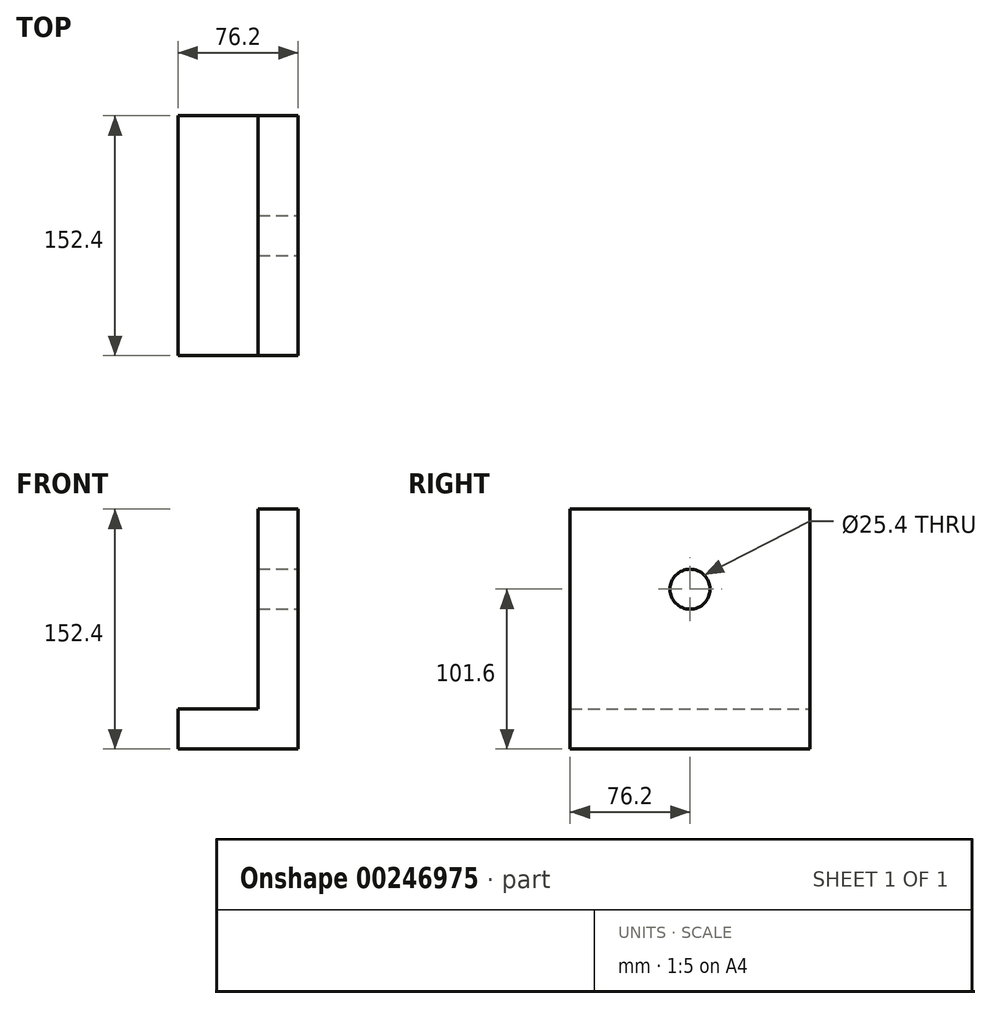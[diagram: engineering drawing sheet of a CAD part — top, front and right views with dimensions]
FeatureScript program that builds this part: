
annotation { "Feature Type Name" : "Feature", "Feature Type Description" : "" }
export const myFeature = defineFeature(function(context is Context, id is Id, definition is map)
    precondition{}
    {
        {
            var Q0;
            Q0=qCreatedBy(makeId("Front.planeOp"),FACE);
            var sketch = newSketch(context, id + "F0", { "sketchPlane" : qUnion([Q0])});
            skLineSegment(sketch, "E0", {"start": v(0, 0) * mm, "end": v(-76.2, 0) * mm});
            skLineSegment(sketch, "E1", {"start": v(-76.2, 0) * mm, "end": v(-76.2, 25.4) * mm});
            skLineSegment(sketch, "E2", {"start": v(-76.2, 25.4) * mm, "end": v(-25.4, 25.4) * mm});
            skLineSegment(sketch, "E3", {"start": v(-25.4, 25.4) * mm, "end": v(-25.4, 152.4) * mm});
            skLineSegment(sketch, "E4", {"start": v(-25.4, 152.4) * mm, "end": v(0, 152.4) * mm});
            skLineSegment(sketch, "E5", {"start": v(0, 152.4) * mm, "end": v(0, 0) * mm});
            skSolve(sketch);
        }
        {
            var Q0;
            Q0=makeQuery(id+"F0.imprint","IMPRINT",FACE,{"disambiguationData":[TD([[makeQuery(id+"F0.imprint","IMPRINT",EDGE,{"derivedFrom":sQuery(id+"F0.wireOp",EDGE,"E0")}),-1.0]])]});
            extrude(context, id + "F1", {"entities" : qUnion([Q0]), "endBound" : BoundingType.SYMMETRIC, "depth" : 152.4 * mm});
        }
        {
            var Q0;
            Q0=makeQuery(id+"F1.opExtrude","SWEPT_FACE",FACE,{"disambiguationData":[OSD([sQuery(id+"F0.wireOp",EDGE,"E5")])]});
            var sketch = newSketch(context, id + "F2", { "sketchPlane" : qUnion([Q0])});
            skCircle(sketch, "E6", {"center": v(0, 101.6) * mm, "radius": 12.7 * mm});
            skSolve(sketch);
        }
        {
            var Q0;
            Q0 = qSketchRegion(id + "F2", true);
            extrude(context, id + "F3", {"entities" : qUnion([Q0]), "operationType" : NewBodyOperationType.REMOVE, "oppositeDirection" : true, "depth" : 87.63 * mm});
        }
    });
